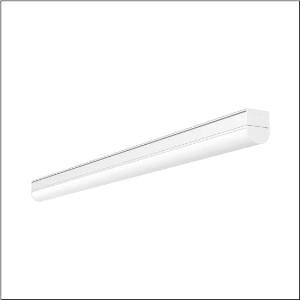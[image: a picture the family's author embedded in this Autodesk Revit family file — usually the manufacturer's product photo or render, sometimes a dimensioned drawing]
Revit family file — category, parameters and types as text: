
# Revit family: ecopack_r__31_51lj12mnm70a_41d1
name_source: partatom
category: Lighting Fixtures
units: mm (PartAtom-declared; Revit-internal decimal feet)

## family parameters
Cut with Voids When Loaded = No
Host = Face
Light Source = No
Part Type = Normal
Room Calculation Point = No
Round Connector Dimension = Use Diameter
Shared = No

## types (1)
- --- (1 x LED, 6780 lm, 50 W, 5000K)
    Apparent Load = 50 VA
    CIE Flux Codes = 39 67 87 89 100
    Color Rendering = 80
    Color Temperature = 5000K
    Default Elevation = 1800 mm
    Description = Ecopack® 31, diffuser luminaire, primary optical cover: cover, of PC, frosted, light emission: direct distribution, primary light characteristic: symmetric, installation type: surface-mounted, LED, rated luminous flux: 7.000lm, luminous efficacy: 140lm/W, light colour: 830/840/850, colour temperature: 3000/4000/5000K, control gear: ECG, with terminal, 3-pole, mains connection: 220..240V, AC, 50/60Hz, rated input power: 50W, housing, of aluminium, traffic white (RAL 9016), length: 1.450mm, width: 56mm, height: 68mm, end cap, of PC, white, protection rating (complete): IP20, insulation class (complete): insulation class I (protective earthing), certification: CE, impact resistance: IK06, permissible operating ambient temperature: -20..+40°C, packaging unit: 1 piece
    Height = 68 mm
    Lamp = 1 x LED
    Lamp Light Flux = 6780 lm
    Lamp Power = 50 W
    Lamp count = 1
    Length = 1450 mm
    Luminous efficacy = 136 lm/W
    Manufacturer = Siteco
    ModVariant = No
    Model = 51LJ12MNM70A
    Mounting Place = Ceiling
    Mounting Type = Surface mounted
    Number of Poles = 1
    OnlyDefault = Yes
    Power Factor = 1
    Product Name = Ecopack® 31
    Product group = diffuser luminaire
    ProductGroupID = 305
    Protection Class = Protection class I
    Protection Degree = IP 20
    RLX_Detail_Level = 1
    RLX_Emergency_Light_Flux = 0 lm
    RLX_Emergency_Type = 0
    RLX_Emergency_Type_DB = No
    RlxData = <blob elided: 39293 chars, md5=f681182a>
    Socket = socket
    Standby Power = 0 W
    System Light Flux = 6780 lm
    System Power = 50 W
    Type Comments = individual setting: colour temperature 5000K, luminous flux: 100 % | (ON | ON)
    Type Image = l_1007033.jpg
    URL = http://relux.com
    VarID = @adj_145083
    Voltage = 0 V
    Weight = 0.00 kg
    Width = 56 mm

## geometry (parser evidence)
native form markers: Blend x4, Sweep x11
no freeform markers — native parametric forms only
